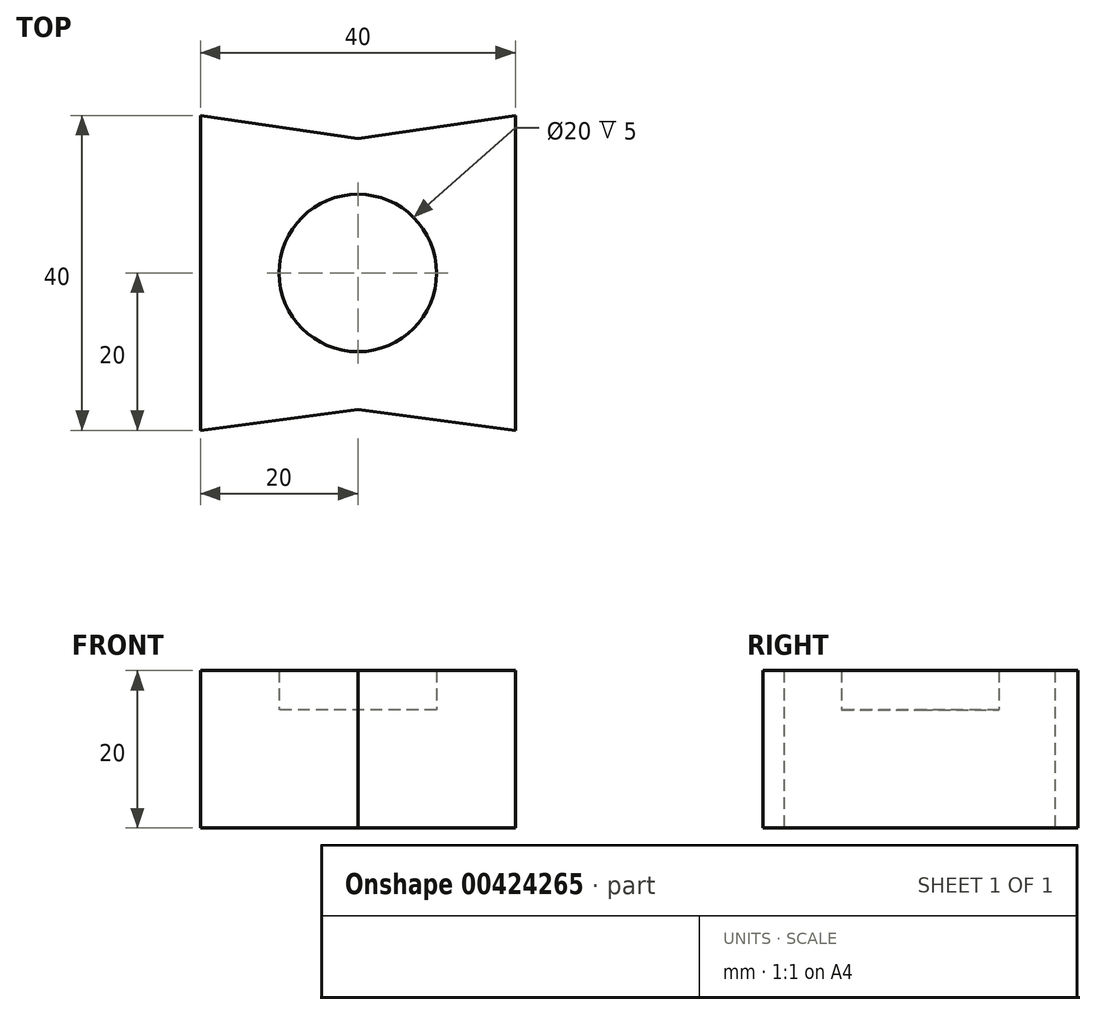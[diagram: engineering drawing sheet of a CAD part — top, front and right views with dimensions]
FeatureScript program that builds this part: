
annotation { "Feature Type Name" : "Feature", "Feature Type Description" : "" }
export const myFeature = defineFeature(function(context is Context, id is Id, definition is map)
    precondition{}
    {
        {
            var Q0;
            Q0=qCreatedBy(makeId("Top.planeOp"),FACE);
            var sketch = newSketch(context, id + "F0", { "sketchPlane" : qUnion([Q0])});
            skLineSegment(sketch, "E0", {"start": v(-20, 0) * mm, "end": v(-20, 20) * mm});
            skLineSegment(sketch, "E1.left", {"start": v(-20, 20) * mm, "end": v(-20, -20) * mm});
            skLineSegment(sketch, "E1.right", {"start": v(20, 20) * mm, "end": v(20, -20) * mm});
            skPoint(sketch, "E1.middle", {"position": v(0, 0) * mm});
            skLineSegment(sketch, "E2", {"start": v(-20, 20) * mm, "end": v(0, 17.1) * mm});
            skLineSegment(sketch, "E3", {"start": v(0, 17.1) * mm, "end": v(20, 20) * mm});
            skLineSegment(sketch, "E4", {"start": v(20, -20) * mm, "end": v(0, -17.32) * mm});
            skLineSegment(sketch, "E5", {"start": v(0, -17.32) * mm, "end": v(-20, -20) * mm});
            skSolve(sketch);
        }
        {
            var Q0;
            Q0=makeQuery(id+"F0.imprint","IMPRINT",FACE,{"disambiguationData":[TD([[makeQuery(id+"F0.imprint","IMPRINT",EDGE,{"derivedFrom":sQuery(id+"F0.wireOp",EDGE,"E1.right")}),-1.0]])]});
            extrude(context, id + "F1", {"entities" : qUnion([Q0]), "depth" : 15 * mm, "offsetDistance" : 25 * mm});
        }
        {
            var Q0;
            Q0=makeQuery(id+"F1.opExtrude","CAP_FACE",FACE,{"disambiguationData":[OSD([sQuery(id+"F0.wireOp",EDGE,"E1.left"),sQuery(id+"F0.wireOp",EDGE,"E1.right"),sQuery(id+"F0.wireOp",EDGE,"E2"),sQuery(id+"F0.wireOp",EDGE,"E3"),sQuery(id+"F0.wireOp",EDGE,"E4"),sQuery(id+"F0.wireOp",EDGE,"E5")])],"isStart":false});
            var sketch = newSketch(context, id + "F2", { "sketchPlane" : qUnion([Q0])});
            skLineSegment(sketch, "E6", {"start": v(0, 0) * mm, "end": v(10, 0) * mm});
            skCircle(sketch, "E7", {"center": v(0, 0) * mm, "radius": 10 * mm});
            skSolve(sketch);
        }
        {
            var Q0;
            Q0=makeQuery(id+"F2.imprint","IMPRINT",FACE,{"disambiguationData":[TD([[makeQuery(id+"F2.imprint","IMPRINT",EDGE,{"derivedFrom":sQuery(id+"F2.wireOp",EDGE,"E7")}),-1.0]])]});
            extrude(context, id + "F3", {"entities" : qUnion([Q0]), "operationType" : NewBodyOperationType.ADD, "depth" : 5 * mm, "offsetDistance" : 25 * mm});
        }
    });
